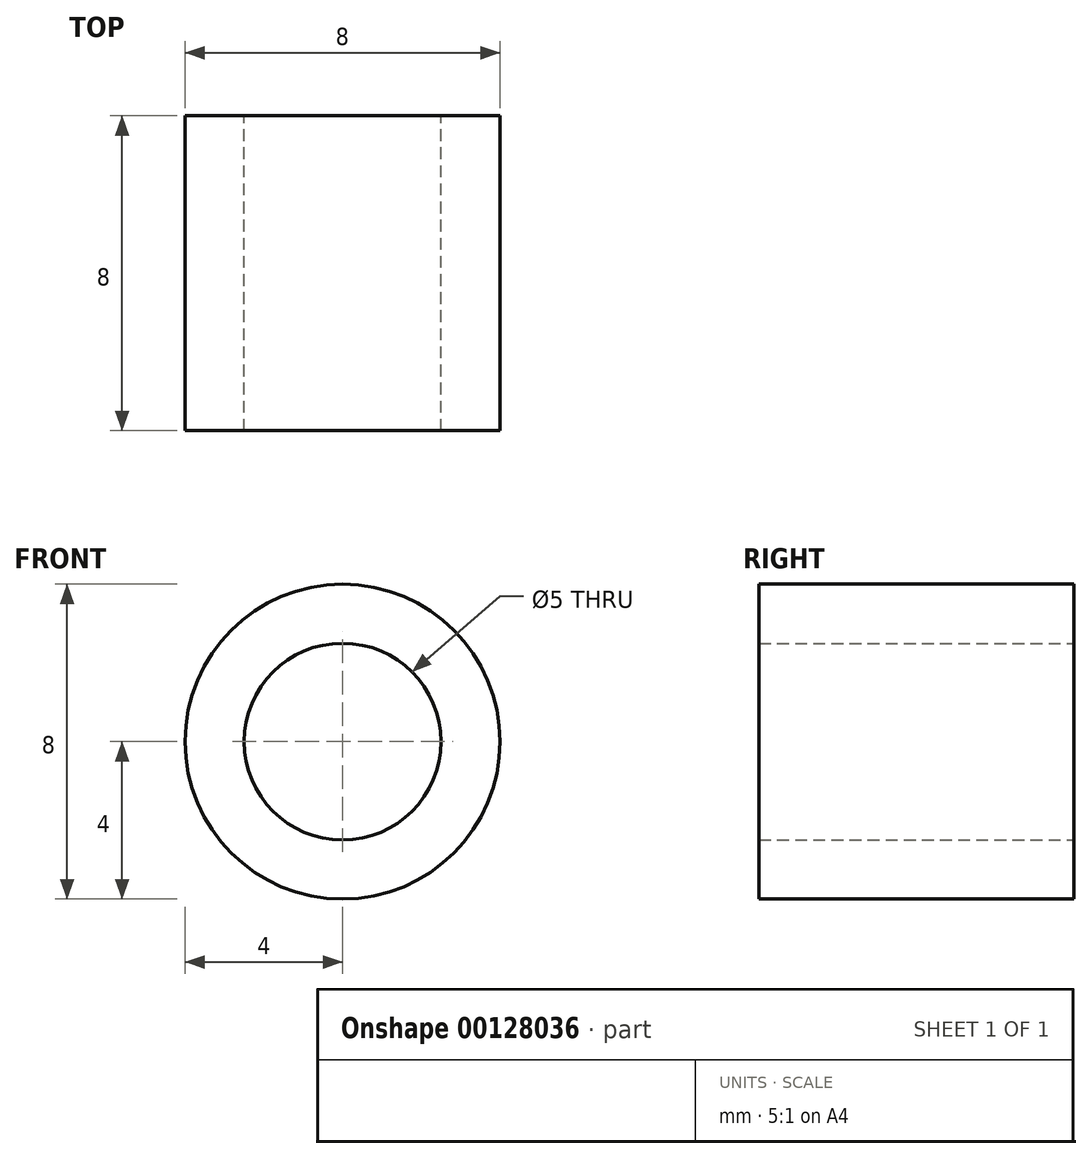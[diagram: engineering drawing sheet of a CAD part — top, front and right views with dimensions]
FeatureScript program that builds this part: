
annotation { "Feature Type Name" : "Feature", "Feature Type Description" : "" }
export const myFeature = defineFeature(function(context is Context, id is Id, definition is map)
    precondition{}
    {
        {
            var Q0;
            Q0=qCreatedBy(makeId("Front.planeOp"),FACE);
            var sketch = newSketch(context, id + "F0", { "sketchPlane" : qUnion([Q0])});
            skCircle(sketch, "E0", {"center": v(0, 0) * mm, "radius": 2.5 * mm});
            skCircle(sketch, "E1", {"center": v(0, 0) * mm, "radius": 4 * mm});
            skSolve(sketch);
        }
        {
            var Q0;
            Q0 = qSketchRegion(id + "F0", true);
            extrude(context, id + "F1", {"entities" : qUnion([Q0]), "depth" : 8 * mm});
        }
    });
